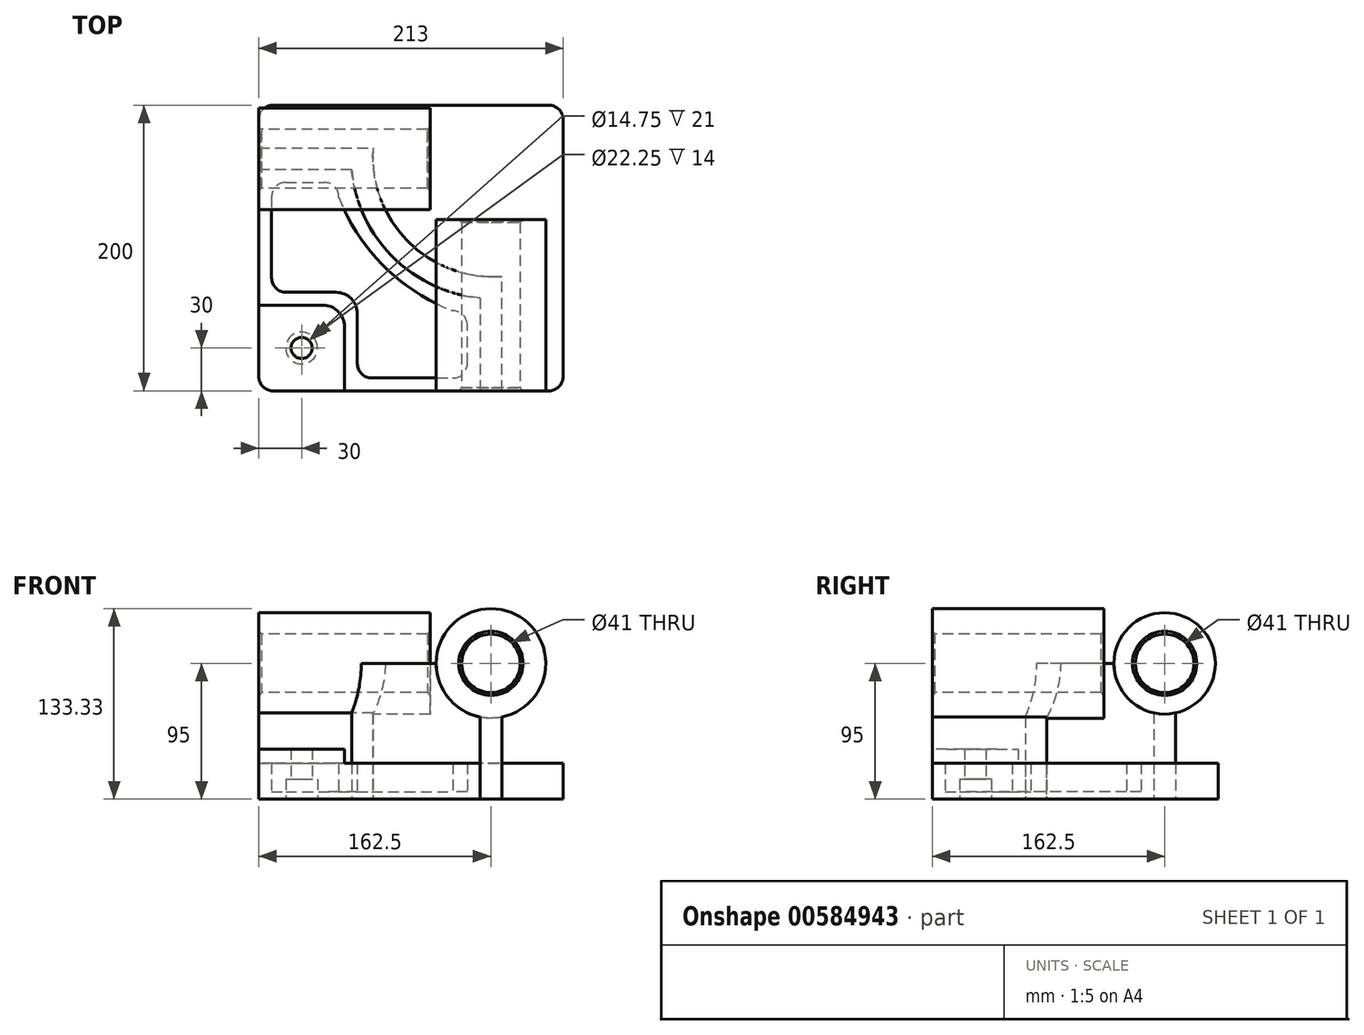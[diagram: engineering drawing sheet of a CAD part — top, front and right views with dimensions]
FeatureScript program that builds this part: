
annotation { "Feature Type Name" : "Feature", "Feature Type Description" : "" }
export const myFeature = defineFeature(function(context is Context, id is Id, definition is map)
    precondition{}
    {
        {
            var Q0;
            Q0=qCreatedBy(makeId("Top.planeOp"),FACE);
            var sketch = newSketch(context, id + "F0", { "sketchPlane" : qUnion([Q0])});
            skLineSegment(sketch, "E0.bottom", {"start": v(96.5, -100) * mm, "end": v(-96.5, -100) * mm});
            skLineSegment(sketch, "E0.top", {"start": v(96.5, 100) * mm, "end": v(-96.5, 100) * mm});
            skLineSegment(sketch, "E0.left", {"start": v(106.5, -90) * mm, "end": v(106.5, 90) * mm});
            skLineSegment(sketch, "E0.right", {"start": v(-106.5, -90) * mm, "end": v(-106.5, 90) * mm});
            skPoint(sketch, "E0.middle", {"position": v(0, 0) * mm});
            skPoint(sketch, "E1.visualSharp", {"position": v(-106.5, 100) * mm});
            skArc(sketch, "E1.filletArc", {"start": v(-96.5, 100) * mm, "mid": v(-103.57, 97.07) * mm, "end": v(-106.5, 90) * mm});
            skPoint(sketch, "E2.visualSharp", {"position": v(106.5, 100) * mm});
            skArc(sketch, "E2.filletArc", {"start": v(106.5, 90) * mm, "mid": v(103.57, 97.07) * mm, "end": v(96.5, 100) * mm});
            skPoint(sketch, "E3.visualSharp", {"position": v(106.5, -100) * mm});
            skArc(sketch, "E3.filletArc", {"start": v(96.5, -100) * mm, "mid": v(103.57, -97.07) * mm, "end": v(106.5, -90) * mm});
            skPoint(sketch, "E4.visualSharp", {"position": v(-106.5, -100) * mm});
            skArc(sketch, "E4.filletArc", {"start": v(-106.5, -90) * mm, "mid": v(-103.57, -97.07) * mm, "end": v(-96.5, -100) * mm});
            skLineSegment(sketch, "E5", {"start": v(-106.5, -40) * mm, "end": v(-61.5, -40) * mm});
            skLineSegment(sketch, "E6", {"start": v(-46.5, -55) * mm, "end": v(-46.5, -100) * mm});
            skPoint(sketch, "E7.visualSharp", {"position": v(-46.5, -40) * mm});
            skArc(sketch, "E7.filletArc", {"start": v(-46.5, -55) * mm, "mid": v(-50.9, -44.4) * mm, "end": v(-61.5, -40) * mm});
            skPoint(sketch, "E8", {"position": v(-76.5, -70) * mm});
            skLineSegment(sketch, "E9", {"start": v(-106.5, 0) * mm, "end": v(-97.5, 0) * mm, "construction": true});
            skPoint(sketch, "E9.endSnap0", {"position": v(-106.5, 0) * mm});
            skLineSegment(sketch, "E10", {"start": v(-84, -40) * mm, "end": v(-84, -31) * mm, "construction": true});
            skLineSegment(sketch, "E11", {"start": v(-46.5, -77.5) * mm, "end": v(-37.5, -77.5) * mm, "construction": true});
            skLineSegment(sketch, "E12", {"start": v(0, -100) * mm, "end": v(0, -91) * mm, "construction": true});
            skPoint(sketch, "E13", {"position": v(-97.5, 46) * mm});
            skLineSegment(sketch, "E14", {"start": v(-97.5, 36) * mm, "end": v(-97.5, -21) * mm});
            skLineSegment(sketch, "E15", {"start": v(-87.5, -31) * mm, "end": v(-52.5, -31) * mm});
            skLineSegment(sketch, "E16", {"start": v(-37.5, -46) * mm, "end": v(-37.5, -81) * mm});
            skPoint(sketch, "E17", {"position": v(39.5, -91) * mm});
            skLineSegment(sketch, "E18", {"start": v(-27.5, -91) * mm, "end": v(29.5, -91) * mm});
            skPoint(sketch, "E19.visualSharp", {"position": v(-37.5, -31) * mm});
            skArc(sketch, "E19.filletArc", {"start": v(-37.5, -46) * mm, "mid": v(-41.9, -35.4) * mm, "end": v(-52.5, -31) * mm});
            skPoint(sketch, "E20", {"position": v(-50.5, 46) * mm});
            skPoint(sketch, "E21", {"position": v(39.5, -44) * mm});
            skLineSegment(sketch, "E22", {"start": v(-87.5, 46) * mm, "end": v(-60.5, 46) * mm});
            skLineSegment(sketch, "E23", {"start": v(39.5, -81) * mm, "end": v(39.5, -54) * mm});
            skLineSegment(sketch, "E24", {"start": v(29.5, -44) * mm, "end": v(29.5, -44) * mm});
            skLineSegment(sketch, "E25", {"start": v(-50.5, 35.82) * mm, "end": v(-50.5, 36) * mm});
            skArc(sketch, "E26.filletArc", {"start": v(-50.5, 36) * mm, "mid": v(-53.43, 43.07) * mm, "end": v(-60.5, 46) * mm});
            skArc(sketch, "E27.filletArc", {"start": v(-87.5, 46) * mm, "mid": v(-94.57, 43.07) * mm, "end": v(-97.5, 36) * mm});
            skPoint(sketch, "E28.visualSharp", {"position": v(-97.5, -31) * mm});
            skArc(sketch, "E28.filletArc", {"start": v(-97.5, -21) * mm, "mid": v(-94.57, -28.07) * mm, "end": v(-87.5, -31) * mm});
            skPoint(sketch, "E29.visualSharp", {"position": v(-37.5, -91) * mm});
            skArc(sketch, "E29.filletArc", {"start": v(-37.5, -81) * mm, "mid": v(-34.57, -88.07) * mm, "end": v(-27.5, -91) * mm});
            skArc(sketch, "E30.filletArc", {"start": v(29.5, -91) * mm, "mid": v(36.57, -88.07) * mm, "end": v(39.5, -81) * mm});
            skArc(sketch, "E31.filletArc", {"start": v(39.5, -54) * mm, "mid": v(36.57, -46.93) * mm, "end": v(29.5, -44) * mm});
            skPoint(sketch, "E32.visualSharp", {"position": v(-50.5, -44) * mm});
            skPoint(sketch, "E33", {"position": v(-106.5, 55) * mm});
            skPoint(sketch, "E34", {"position": v(-106.5, 70) * mm});
            skPoint(sketch, "E35", {"position": v(48.5, -100) * mm});
            skPoint(sketch, "E36", {"position": v(63.5, -100) * mm});
            skPoint(sketch, "E37", {"position": v(-26.5, 70) * mm});
            skPoint(sketch, "E38", {"position": v(63.5, -20) * mm});
            skPoint(sketch, "E39", {"position": v(-41.5, 55) * mm});
            skPoint(sketch, "E40", {"position": v(48.5, -35) * mm});
            skLineSegment(sketch, "E41", {"start": v(-106.5, 55) * mm, "end": v(-41.5, 55) * mm});
            skLineSegment(sketch, "E42", {"start": v(-106.5, 70) * mm, "end": v(-26.5, 70) * mm});
            skLineSegment(sketch, "E43", {"start": v(63.5, -100) * mm, "end": v(63.5, -20) * mm});
            skLineSegment(sketch, "E44", {"start": v(48.5, -100) * mm, "end": v(48.5, -35) * mm});
            skPoint(sketch, "E45.visualSharp", {"position": v(-41.5, -35) * mm});
            skPoint(sketch, "E46.visualSharp", {"position": v(-26.5, -20) * mm});
            skArc(sketch, "E47", {"start": v(-26.5, 70) * mm, "mid": v(-1.92, 4.58) * mm, "end": v(63.5, -20) * mm});
            skArc(sketch, "E48", {"start": v(-41.5, 55) * mm, "mid": v(-12.73, -6.23) * mm, "end": v(48.5, -35) * mm});
            skArc(sketch, "E49", {"start": v(-50.5, 35.82) * mm, "mid": v(-19.04, -12.65) * mm, "end": v(29.5, -44) * mm});
            skSolve(sketch);
        }
        {
            var Q0;
            {var subQ1=sQuery(id+"F0.wireOp",EDGE,"E4.filletArc");Q0=makeQuery(id+"F0.imprint","IMPRINT",FACE,{"disambiguationData":[TD([[makeQuery(id+"F0.imprint","IMPRINT",EDGE,{"derivedFrom":subQ1}),1.0]])]});}
            extrude(context, id + "F1", {"entities" : qUnion([Q0]), "depth" : 35 * mm, "offsetDistance" : 25 * mm});
        }
        {
            var Q0;
            {var subQ3=sQuery(id+"F0.wireOp",EDGE,"E5");Q0=makeQuery(id+"F0.imprint","IMPRINT",FACE,{"disambiguationData":[TD([[makeQuery(id+"F0.imprint","IMPRINT",EDGE,{"derivedFrom":subQ3}),1.0]])]});}
            var Q1;
            Q1=makeQuery(id+"F0.imprint","IMPRINT",FACE,{"disambiguationData":[TD([[makeQuery(id+"F0.imprint","IMPRINT",EDGE,{"derivedFrom":sQuery(id+"F0.wireOp",EDGE,"E0.top")}),1.0]])]});
            extrude(context, id + "F2", {"entities" : qUnion([Q0, Q1]), "operationType" : NewBodyOperationType.ADD, "depth" : 25 * mm, "offsetDistance" : 25 * mm});
        }
        {
            var Q0;
            {var subQ3=sQuery(id+"F0.wireOp",EDGE,"E41");Q0=makeQuery(id+"F0.imprint","IMPRINT",FACE,{"disambiguationData":[TD([[makeQuery(id+"F0.imprint","IMPRINT",EDGE,{"derivedFrom":subQ3}),1.0]])]});}
            extrude(context, id + "F3", {"entities" : qUnion([Q0]), "depth" : 95 * mm, "offsetDistance" : 25 * mm});
        }
        {
            var Q0;
            Q0=makeQuery(id+"F0.imprint","IMPRINT",FACE,{"disambiguationData":[TD([[makeQuery(id+"F0.imprint","IMPRINT",EDGE,{"derivedFrom":sQuery(id+"F0.wireOp",EDGE,"E14")}),1.0]])]});
            extrude(context, id + "F4", {"entities" : qUnion([Q0]), "operationType" : NewBodyOperationType.ADD, "depth" : 5 * mm, "offsetDistance" : 25 * mm});
        }
        {
            var Q0;
            Q0=sQuery(id+"F0.wireOp",VERTEX,"E8");
            var Q1;
            Q1=makeQuery(id+"F1.opExtrude","SWEPT_BODY",BODY,{"disambiguationData":[OSD([sQuery(id+"F0.wireOp",EDGE,"E0.bottom"),sQuery(id+"F0.wireOp",EDGE,"E0.right"),sQuery(id+"F0.wireOp",EDGE,"E4.filletArc"),sQuery(id+"F0.wireOp",EDGE,"E5"),sQuery(id+"F0.wireOp",EDGE,"E6"),sQuery(id+"F0.wireOp",EDGE,"E7.filletArc")])]});
            hole(context, id + "F5", {"style" : HoleStyle.C_BORE, "endStyle" : HoleEndStyle.THROUGH, "oppositeDirection" : true, "standardTappedOrClearance" : lookupTablePath({ "standard" : "ISO", "fit" : "Close", "size" : "M14", "type" : "Clearance" }), "standardBlindInLast" : lookupTablePath({ "fit" : "Close", "standard" : "ISO", "size" : "M14", "type" : "Clearance" }), "holeDiameter" : 14.75 * mm, "cBoreDiameter" : 22.25 * mm, "cBoreDepth" : 14 * mm, "majorDiameter" : 5 * mm, "isTappedThrough" : true, "tappedDepth" : 12 * mm, "tapClearance" : 3, "locations" : qUnion([Q0]), "scope" : qUnion([Q1])});
        }
        {
            var Q0;
            Q0=makeQuery(id+"F3.opExtrude","SWEPT_FACE",FACE,{"disambiguationData":[OSD([sQuery(id+"F0.wireOp",EDGE,"E0.bottom")])]});
            var sketch = newSketch(context, id + "F6", { "sketchPlane" : qUnion([Q0])});
            skLineSegment(sketch, "E50.0", {"start": v(63.5, 95) * mm, "end": v(48.5, 95) * mm});
            skCircle(sketch, "E51", {"center": v(56, 95) * mm, "radius": 20.5 * mm});
            skCircle(sketch, "E52", {"center": v(56, 95) * mm, "radius": 38.33 * mm});
            skSolve(sketch);
        }
        {
            var Q0;
            {var subQ0=sQuery(id+"F6.wireOp",EDGE,"E50.0");Q0=makeQuery(id+"F6.imprint","IMPRINT",FACE,{"disambiguationData":[TD([[makeQuery(id+"F6.imprint","IMPRINT",EDGE,{"derivedFrom":subQ0}),1.0]])]});}
            var Q1;
            {var subQ0=sQuery(id+"F6.wireOp",EDGE,"E50.0");Q1=makeQuery(id+"F6.imprint","IMPRINT",FACE,{"disambiguationData":[TD([[makeQuery(id+"F6.imprint","IMPRINT",EDGE,{"derivedFrom":subQ0}),-1.0]])]});}
            extrude(context, id + "F7", {"entities" : qUnion([Q0, Q1]), "operationType" : NewBodyOperationType.REMOVE, "oppositeDirection" : true, "depth" : 120 * mm, "offsetDistance" : 25 * mm});
        }
        {
            var Q0;
            {var subQ0=sQuery(id+"F6.wireOp",EDGE,"E51");var subQ1=sQuery(id+"F0.wireOp",EDGE,"E0.bottom");var subQ2=makeQuery(id+"F3.opExtrude","SWEPT_EDGE",EDGE,{"disambiguationData":[OSD([subQ1,sQuery(id+"F0.wireOp",EDGE,"E43")])]});var subQ3=makeQuery(id+"F6.imprint","INTERSECT",VERTEX,{"derivedFrom":[subQ2,subQ0]});Q0=makeQuery(id+"F6.imprint","IMPRINT",FACE,{"disambiguationData":[TD([[makeQuery(id+"F6.imprint","IMPRINT",EDGE,{"disambiguationData":[TD([[subQ3,-1.0]])],"derivedFrom":subQ0}),-1.0]])]});}
            var Q1;
            {var subQ0=sQuery(id+"F6.wireOp",EDGE,"E51");var subQ1=sQuery(id+"F0.wireOp",EDGE,"E0.bottom");var subQ2=makeQuery(id+"F3.opExtrude","SWEPT_EDGE",EDGE,{"disambiguationData":[OSD([subQ1,sQuery(id+"F0.wireOp",EDGE,"E43")])]});var subQ3=makeQuery(id+"F6.imprint","INTERSECT",VERTEX,{"derivedFrom":[subQ2,subQ0]});Q1=makeQuery(id+"F6.imprint","IMPRINT",FACE,{"disambiguationData":[TD([[makeQuery(id+"F6.imprint","IMPRINT",EDGE,{"disambiguationData":[TD([[subQ3,1.0]])],"derivedFrom":subQ0}),-1.0]])]});}
            extrude(context, id + "F8", {"entities" : qUnion([Q0, Q1]), "operationType" : NewBodyOperationType.ADD, "oppositeDirection" : true, "depth" : 120 * mm, "offsetDistance" : 25 * mm});
        }
        {
            var Q0;
            Q0=makeQuery(id+"F3.opExtrude","SWEPT_FACE",FACE,{"disambiguationData":[OSD([sQuery(id+"F0.wireOp",EDGE,"E0.right")])]});
            var sketch = newSketch(context, id + "F9", { "sketchPlane" : qUnion([Q0])});
            skLineSegment(sketch, "E53.0", {"start": v(-55, 95) * mm, "end": v(-70, 95) * mm});
            skCircle(sketch, "E54", {"center": v(-62.5, 95) * mm, "radius": 20.5 * mm});
            skCircle(sketch, "E55", {"center": v(-62.5, 95) * mm, "radius": 35.5 * mm});
            skSolve(sketch);
        }
        {
            var Q0;
            {var subQ0=sQuery(id+"F9.wireOp",EDGE,"E53.0");Q0=makeQuery(id+"F9.imprint","IMPRINT",FACE,{"disambiguationData":[TD([[makeQuery(id+"F9.imprint","IMPRINT",EDGE,{"derivedFrom":subQ0}),1.0]])]});}
            var Q1;
            {var subQ0=sQuery(id+"F9.wireOp",EDGE,"E53.0");Q1=makeQuery(id+"F9.imprint","IMPRINT",FACE,{"disambiguationData":[TD([[makeQuery(id+"F9.imprint","IMPRINT",EDGE,{"derivedFrom":subQ0}),-1.0]])]});}
            extrude(context, id + "F10", {"entities" : qUnion([Q0, Q1]), "operationType" : NewBodyOperationType.REMOVE, "oppositeDirection" : true, "depth" : 120 * mm, "offsetDistance" : 25 * mm});
        }
        {
            var Q0;
            {var subQ0=sQuery(id+"F9.wireOp",EDGE,"E54");var subQ1=sQuery(id+"F0.wireOp",EDGE,"E0.right");var subQ2=makeQuery(id+"F3.opExtrude","SWEPT_EDGE",EDGE,{"disambiguationData":[OSD([subQ1,sQuery(id+"F0.wireOp",EDGE,"E41")])]});var subQ3=makeQuery(id+"F9.imprint","INTERSECT",VERTEX,{"derivedFrom":[subQ2,subQ0]});Q0=makeQuery(id+"F9.imprint","IMPRINT",FACE,{"disambiguationData":[TD([[makeQuery(id+"F9.imprint","IMPRINT",EDGE,{"disambiguationData":[TD([[subQ3,-1.0]])],"derivedFrom":subQ0}),-1.0]])]});}
            var Q1;
            {var subQ0=sQuery(id+"F9.wireOp",EDGE,"E54");var subQ1=sQuery(id+"F0.wireOp",EDGE,"E0.right");var subQ2=makeQuery(id+"F3.opExtrude","SWEPT_EDGE",EDGE,{"disambiguationData":[OSD([subQ1,sQuery(id+"F0.wireOp",EDGE,"E41")])]});var subQ3=makeQuery(id+"F9.imprint","INTERSECT",VERTEX,{"derivedFrom":[subQ2,subQ0]});Q1=makeQuery(id+"F9.imprint","IMPRINT",FACE,{"disambiguationData":[TD([[makeQuery(id+"F9.imprint","IMPRINT",EDGE,{"disambiguationData":[TD([[subQ3,1.0]])],"derivedFrom":subQ0}),-1.0]])]});}
            extrude(context, id + "F11", {"entities" : qUnion([Q0, Q1]), "operationType" : NewBodyOperationType.ADD, "oppositeDirection" : true, "depth" : 120 * mm, "offsetDistance" : 25 * mm});
        }
        {
            var Q0;
            {var subQ0=sQuery(id+"F9.wireOp",EDGE,"E54");Q0=makeQuery(id+"F11.boolean.opBoolean","MERGE",EDGE,{"derivedFrom":[makeQuery(id+"F10.boolean.opBoolean","COPY",EDGE,{"derivedFrom":makeQuery(id+"F10.opExtrude","CAP_EDGE",EDGE,{"disambiguationData":[OSD([subQ0])],"isStart":true})}),makeQuery(id+"F11.opExtrude","CAP_EDGE",EDGE,{"disambiguationData":[OSD([subQ0])],"isStart":true})]});}
            var Q1;
            Q1=makeQuery(id+"F11.opExtrude","CAP_EDGE",EDGE,{"disambiguationData":[OSD([sQuery(id+"F9.wireOp",EDGE,"E54")])],"isStart":false});
            var Q2;
            Q2=makeQuery(id+"F8.opExtrude","CAP_EDGE",EDGE,{"disambiguationData":[OSD([sQuery(id+"F6.wireOp",EDGE,"E51")])],"isStart":false});
            var Q3;
            {var subQ0=sQuery(id+"F6.wireOp",EDGE,"E51");Q3=makeQuery(id+"F8.boolean.opBoolean","MERGE",EDGE,{"derivedFrom":[makeQuery(id+"F7.boolean.opBoolean","COPY",EDGE,{"derivedFrom":makeQuery(id+"F7.opExtrude","CAP_EDGE",EDGE,{"disambiguationData":[OSD([subQ0])],"isStart":true})}),makeQuery(id+"F8.opExtrude","CAP_EDGE",EDGE,{"disambiguationData":[OSD([subQ0])],"isStart":true})]});}
            chamfer(context, id + "F12", {"entities" : qUnion([Q0, Q1, Q2, Q3]), "chamferType" : ChamferType.OFFSET_ANGLE, "width" : 2 * mm, "oppositeDirection" : false, "angle" : 45 * degree, "tangentPropagation" : true});
        }
    });
